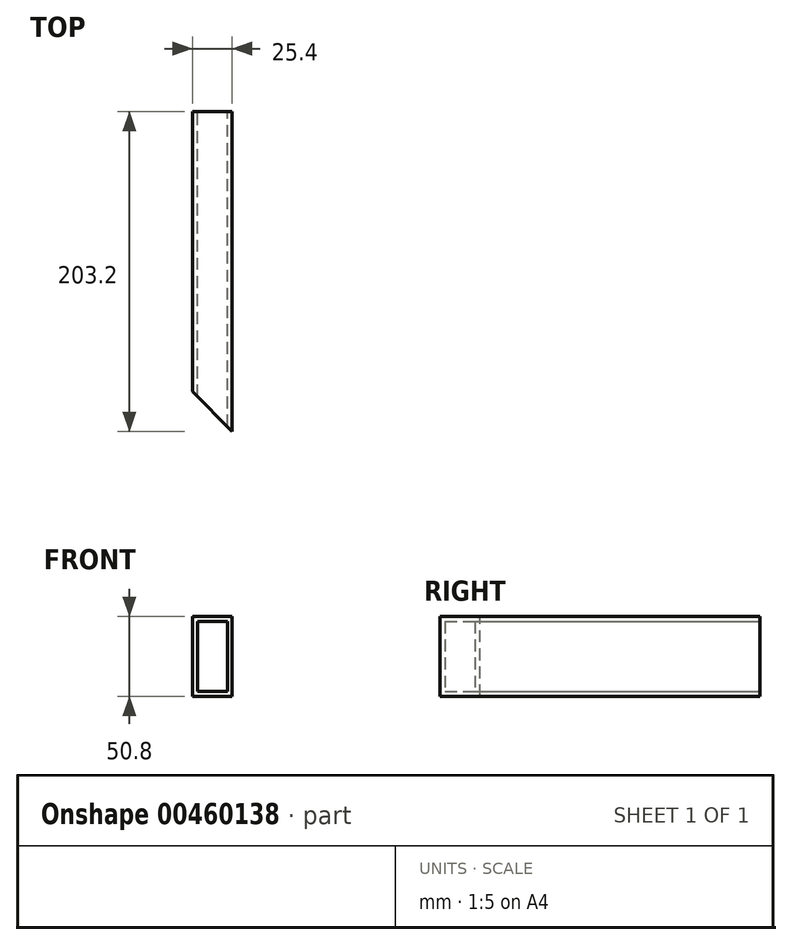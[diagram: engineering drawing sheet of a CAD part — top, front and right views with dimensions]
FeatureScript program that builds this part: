
annotation { "Feature Type Name" : "Feature", "Feature Type Description" : "" }
export const myFeature = defineFeature(function(context is Context, id is Id, definition is map)
    precondition{}
    {
        {
            var Q0;
            Q0=qCreatedBy(makeId("Front.planeOp"),FACE);
            var sketch = newSketch(context, id + "F0", { "sketchPlane" : qUnion([Q0])});
            skLineSegment(sketch, "E0.bottom", {"start": v(12.7, 36.51) * mm, "end": v(-12.7, 36.51) * mm});
            skLineSegment(sketch, "E0.top", {"start": v(12.7, -14.29) * mm, "end": v(-12.7, -14.29) * mm});
            skLineSegment(sketch, "E0.left", {"start": v(12.7, 36.51) * mm, "end": v(12.7, -14.29) * mm});
            skLineSegment(sketch, "E0.right", {"start": v(-12.7, 36.51) * mm, "end": v(-12.7, -14.29) * mm});
            skPoint(sketch, "E0.middle", {"position": v(0, 11.11) * mm});
            skLineSegment(sketch, "E1.bottom", {"start": v(9.53, 33.34) * mm, "end": v(-9.52, 33.34) * mm});
            skLineSegment(sketch, "E1.top", {"start": v(9.53, -11.11) * mm, "end": v(-9.52, -11.11) * mm});
            skLineSegment(sketch, "E1.left", {"start": v(9.53, 33.34) * mm, "end": v(9.53, -11.11) * mm});
            skLineSegment(sketch, "E1.right", {"start": v(-9.52, 33.34) * mm, "end": v(-9.52, -11.11) * mm});
            skSolve(sketch);
        }
        {
            var Q0;
            Q0=makeQuery(id+"F0.imprint","IMPRINT",FACE,{"disambiguationData":[TD([[makeQuery(id+"F0.imprint","IMPRINT",EDGE,{"derivedFrom":sQuery(id+"F0.wireOp",EDGE,"E0.bottom")}),1.0]])]});
            extrude(context, id + "F1", {"entities" : qUnion([Q0]), "depth" : 203.2 * mm});
        }
        {
            var Q0;
            Q0=makeQuery(id+"F1.opExtrude","CAP_EDGE",EDGE,{"disambiguationData":[OSD([sQuery(id+"F0.wireOp",EDGE,"E0.right")])],"isStart":false});
            chamfer(context, id + "F2", {"entities" : qUnion([Q0]), "width" : 25.4 * mm, "tangentPropagation" : true});
        }
    });
